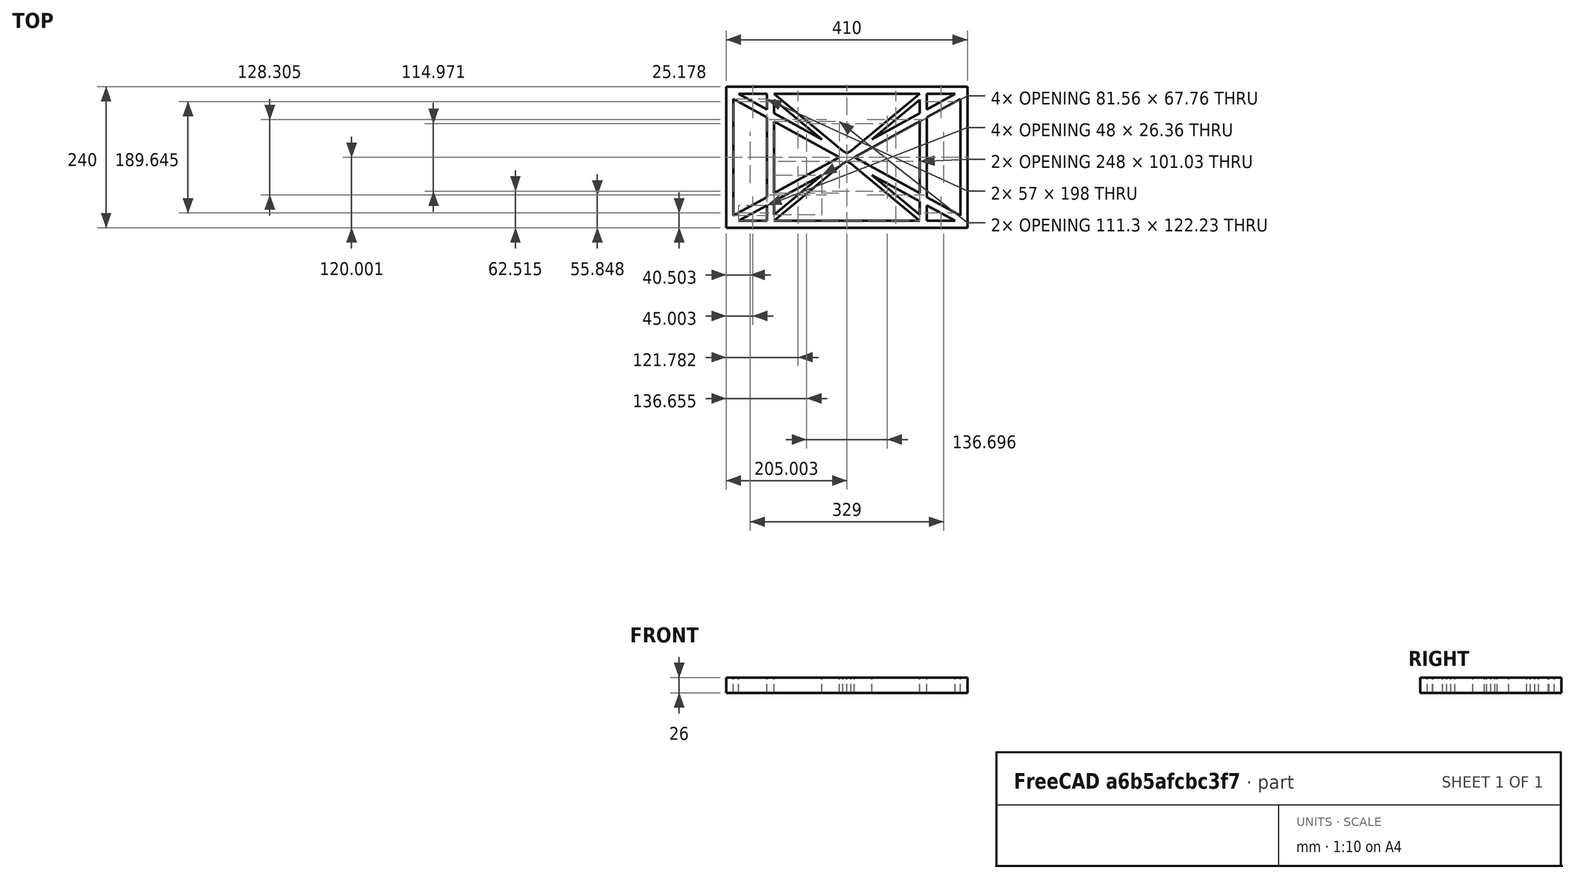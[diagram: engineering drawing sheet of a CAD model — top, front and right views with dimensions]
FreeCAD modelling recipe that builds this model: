
FCSTD DOCUMENT  (FreeCAD 0.19R0.19.2)
Label: laptopStand024
License: All rights reserved
LicenseURL: http://en.wikipedia.org/wiki/All_rights_reserved
objects: Sketcher::SketchObject×3, Part::Extrusion×1
note: 4 computed .brp shape members not serialized (recipe doc carries the construction recipe); baked Part::Feature solids carry a one-line shape summary decoded from their .brp

FEATURE [Sketcher::SketchObject] Sketch
  FullyConstrained = true
  sketch-geometry (52):
    g0: LineSegment StartX=-22.9272 StartY=136.221 StartZ=0 EndX=-22.9272 EndY=-103.779 EndZ=0
    g1: LineSegment StartX=-22.9272 StartY=136.221 StartZ=0 EndX=387.073 EndY=136.221 EndZ=0
    g2: LineSegment StartX=-22.9272 StartY=-103.779 StartZ=0 EndX=387.073 EndY=-103.779 EndZ=0
    g3: LineSegment StartX=387.073 StartY=136.221 StartZ=0 EndX=387.073 EndY=-103.779 EndZ=0
    g4: LineSegment StartX=375.073 StartY=115.221 StartZ=0 EndX=318.073 EndY=83.9235 EndZ=0
    g5: LineSegment StartX=-10.9272 StartY=-82.7794 StartZ=0 EndX=46.0728 EndY=-51.4823 EndZ=0
    g6: LineSegment StartX=-1.92719 StartY=124.221 StartZ=0 EndX=46.0728 EndY=97.8651 EndZ=0
    g7: LineSegment StartX=366.073 StartY=-91.7794 StartZ=0 EndX=318.073 EndY=-65.424 EndZ=0
    g8: LineSegment StartX=-10.9272 StartY=115.221 StartZ=0 EndX=-10.9272 EndY=-82.7794 EndZ=0
    g9: LineSegment StartX=375.073 StartY=-82.7794 StartZ=0 EndX=375.073 EndY=115.221 EndZ=0
    g10: LineSegment StartX=-1.92719 StartY=-91.7794 StartZ=0 EndX=46.0728 EndY=-91.7794 EndZ=0
    g11: LineSegment StartX=318.073 StartY=124.221 StartZ=0 EndX=366.073 EndY=124.221 EndZ=0
    g12: LineSegment StartX=306.073 StartY=-81.8102 StartZ=0 EndX=224.513 EndY=-14.0532 EndZ=0
    g13: LineSegment StartX=58.0728 StartY=114.251 StartZ=0 EndX=139.632 EndY=46.4944 EndZ=0
    g14: LineSegment StartX=306.073 StartY=124.221 StartZ=0 EndX=189.124 EndY=27.0628 EndZ=0
    g15: LineSegment StartX=58.0728 StartY=-91.7794 StartZ=0 EndX=175.022 EndY=5.37834 EndZ=0
    g16: LineSegment StartX=46.0728 StartY=124.221 StartZ=0 EndX=46.0728 EndY=97.8651 EndZ=0
    g17: LineSegment StartX=58.0728 StartY=-81.8102 StartZ=0 EndX=58.0728 EndY=-58.8351 EndZ=0
    g18: LineSegment StartX=318.073 StartY=124.221 StartZ=0 EndX=318.073 EndY=97.8651 EndZ=0
    g19: LineSegment StartX=306.073 StartY=114.251 StartZ=0 EndX=306.073 EndY=91.2763 EndZ=0
    g20: LineSegment StartX=182.073 StartY=23.1914 StartZ=0 EndX=189.124 EndY=27.0628 EndZ=0
    g21: LineSegment StartX=182.073 StartY=9.24976 StartZ=0 EndX=175.022 EndY=5.37834 EndZ=0
    g22: LineSegment StartX=224.513 StartY=46.4944 StartZ=0 EndX=306.073 EndY=114.251 EndZ=0
    g23: LineSegment StartX=175.022 StartY=27.0628 StartZ=0 EndX=58.0728 EndY=124.221 EndZ=0
    g24: LineSegment StartX=169.377 StartY=16.2206 StartZ=0 EndX=58.0728 EndY=77.3346 EndZ=0
    g25: LineSegment StartX=139.632 StartY=-14.0532 StartZ=0 EndX=58.0728 EndY=-81.8102 EndZ=0
    g26: LineSegment StartX=194.768 StartY=16.2206 StartZ=0 EndX=306.073 EndY=-44.8935 EndZ=0
    g27: LineSegment StartX=224.513 StartY=46.4944 StartZ=0 EndX=306.073 EndY=91.2763 EndZ=0
    g28: LineSegment StartX=175.022 StartY=27.0628 StartZ=0 EndX=182.073 EndY=23.1914 EndZ=0
    g29: LineSegment StartX=139.632 StartY=-14.0532 StartZ=0 EndX=58.0728 EndY=-58.8351 EndZ=0
    g30: LineSegment StartX=189.124 StartY=5.37834 StartZ=0 EndX=182.073 EndY=9.24976 EndZ=0
    g31: LineSegment StartX=189.124 StartY=5.37834 StartZ=0 EndX=306.073 EndY=-91.7794 EndZ=0
    g32: LineSegment StartX=306.073 StartY=77.3346 StartZ=0 EndX=306.073 EndY=-44.8935 EndZ=0
    g33: LineSegment StartX=318.073 StartY=83.9235 StartZ=0 EndX=318.073 EndY=-51.4823 EndZ=0
    g34: LineSegment StartX=318.073 StartY=97.8651 StartZ=0 EndX=366.073 EndY=124.221 EndZ=0
    g35: LineSegment StartX=306.073 StartY=77.3346 StartZ=0 EndX=194.768 EndY=16.2206 EndZ=0
    g36: LineSegment StartX=306.073 StartY=-58.8351 StartZ=0 EndX=224.513 EndY=-14.0532 EndZ=0
    g37: LineSegment StartX=306.073 StartY=-58.8351 StartZ=0 EndX=306.073 EndY=-81.8102 EndZ=0
    g38: LineSegment StartX=318.073 StartY=-51.4823 StartZ=0 EndX=375.073 EndY=-82.7794 EndZ=0
    g39: LineSegment StartX=318.073 StartY=-65.424 StartZ=0 EndX=318.073 EndY=-91.7794 EndZ=0
    g40: LineSegment StartX=306.073 StartY=124.221 StartZ=0 EndX=58.0728 EndY=124.221 EndZ=0
    g41: LineSegment StartX=318.073 StartY=-91.7794 StartZ=0 EndX=366.073 EndY=-91.7794 EndZ=0
    g42: LineSegment StartX=58.0728 StartY=-91.7794 StartZ=0 EndX=306.073 EndY=-91.7794 EndZ=0
    g43: LineSegment StartX=58.0728 StartY=-44.8935 StartZ=0 EndX=58.0728 EndY=77.3346 EndZ=0
    g44: LineSegment StartX=46.0728 StartY=-65.424 StartZ=0 EndX=-1.92719 EndY=-91.7794 EndZ=0
    g45: LineSegment StartX=46.0728 StartY=-65.424 StartZ=0 EndX=46.0728 EndY=-91.7794 EndZ=0
    g46: LineSegment StartX=58.0728 StartY=-44.8935 StartZ=0 EndX=169.377 EndY=16.2206 EndZ=0
    g47: LineSegment StartX=58.0728 StartY=91.2763 StartZ=0 EndX=58.0728 EndY=114.251 EndZ=0
    g48: LineSegment StartX=46.0728 StartY=83.9235 StartZ=0 EndX=46.0728 EndY=-51.4823 EndZ=0
    g49: LineSegment StartX=46.0728 StartY=124.221 StartZ=0 EndX=-1.92719 EndY=124.221 EndZ=0
    g50: LineSegment StartX=58.0728 StartY=91.2763 StartZ=0 EndX=139.632 EndY=46.4944 EndZ=0
    g51: LineSegment StartX=46.0728 StartY=83.9235 StartZ=0 EndX=-10.9272 EndY=115.221 EndZ=0
  constraints (102):
    c: Vertical(g0)
    c: Distance(g0) = 240
    c: Horizontal(g1)
    c: Distance(g1) = 410
    c: Coincident(g1,g0)
    c: Coincident(g2,g0)
    c: Horizontal(g2)
    c: Coincident(g3,g1)
    c: Vertical(g3)
    c: Coincident(g2,g3)
    c: Block(g1)
    c: Horizontal(g10)
    c: Horizontal(g11)
    c: PointOnObject(g35,g6)
    c: Coincident(g28,g20)
    c: Coincident(g30,g21)
    c: Tangent(g7,g24)
    c: PointOnObject(g24,g5)
    c: PointOnObject(g26,g4)
    c: Coincident(g20,g14)
    c: Tangent(g20,g27)
    c: Coincident(g50,g13)
    c: Coincident(g28,g23)
    c: Coincident(g22,g27)
    c: Coincident(g21,g15)
    c: Coincident(g29,g25)
    c: Tangent(g21,g29)
    c: Coincident(g36,g12)
    c: Coincident(g31,g30)
    c: Coincident(g22,g19)
    c: Tangent(g19,g32)
    c: Tangent(g18,g33)
    c: Coincident(g27,g19)
    c: Tangent(g27,g34)
    c: Coincident(g4,g33)
    c: Coincident(g35,g32)
    c: Tangent(g4,g35)
    c: Coincident(g37,g12)
    c: Tangent(g7,g36)
    c: Tangent(g32,g37)
    c: Coincident(g26,g32)
    c: Tangent(g26,g38)
    c: Coincident(g33,g38)
    c: Coincident(g39,g7)
    c: Tangent(g33,g39)
    c: Coincident(g25,g17)
    c: Tangent(g17,g43)
    c: Coincident(g29,g17)
    c: Tangent(g29,g44)
    c: Coincident(g45,g44)
    c: Tangent(g16,g45)
    c: Coincident(g5,g48)
    c: Coincident(g46,g43)
    c: Tangent(g5,g46)
    c: Tangent(g43,g47)
    c: Tangent(g16,g48)
    c: Coincident(g13,g47)
    c: PointOnObject(g40,g23)
    c: Tangent(g40,g49)
    c: Coincident(g6,g16)
    c: Coincident(g50,g47)
    c: Tangent(g6,g50)
    c: Coincident(g24,g43)
    c: Coincident(g51,g48)
    c: Tangent(g24,g51)
    c: Block(g23)
    c: Block(g14)
    c: Block(g20)
    c: Block(g40)
    c: Block(g18)
    c: Block(g34)
    c: Block(g4)
    c: Block(g38)
    c: Block(g9)
    c: Block(g36)
    c: Block(g37)
    c: Block(g7)
    c: Block(g39)
    c: Block(g22)
    c: Block(g31)
    c: Block(g42)
    c: Block(g21)
    c: Block(g15)
    c: Block(g29)
    c: Block(g25)
    c: Block(g45)
    c: Block(g44)
    c: Block(g5)
    c: Block(g8)
    c: Block(g51)
    c: Block(g6)
    c: Block(g16)
    c: Block(g13)
    c: Block(g47)
    c: Block(g35)
    c: Block(g32)
    c: Block(g24)
    c: Block(g46)
    c: Block(g49)
    c: Block(g11)
    c: Block(g41)
    c: Block(g10)
FEATURE [Part::Extrusion] Extrude
  Base = -> Sketch
  Dir = (0,0,1)
  DirMode = 2
  FaceMakerClass = Part::FaceMakerBullseye
  LengthFwd = 26
  LengthRev = 0
  Solid = true
  Symmetric = false
FEATURE [Sketcher::SketchObject] Sketch001
  FullyConstrained = false
  MapMode = 4
  Placement = pos=(0,0,0) rot=(0.57735,0.57735,0.57735;2.0944rad)
  Support = -> [Sketch]
  sketch-geometry (22):
    g0: LineSegment StartX=17.2228 StartY=-16.0875 StartZ=0 EndX=117.223 EndY=-16.0875 EndZ=0
    g1: LineSegment StartX=17.2228 StartY=-16.0875 StartZ=0 EndX=17.2228 EndY=-19.0875 EndZ=0
    g2: LineSegment StartX=117.223 StartY=-16.0875 StartZ=0 EndX=117.223 EndY=-19.0875 EndZ=0
    g3: BSplineCurve PolesCount=3 KnotsCount=2 Degree=2 IsPeriodic=0
    g4: LineSegment StartX=94.6577 StartY=-26.1351 StartZ=0 EndX=24.2583 EndY=-213.335 EndZ=0
    g5: LineSegment StartX=-9.4377 StartY=-200.664 StartZ=0 EndX=24.2583 EndY=-213.335 EndZ=0
    g6: LineSegment StartX=-9.4377 StartY=-200.664 StartZ=0 EndX=56.1962 EndY=-26.1351 EndZ=0
    g7: LineSegment StartX=17.2228 StartY=-19.0875 StartZ=0 EndX=38.8094 EndY=-19.0875 EndZ=0
    g8: BSplineCurve PolesCount=4 KnotsCount=2 Degree=3 IsPeriodic=0
    g9: LineSegment StartX=78.0148 StartY=-19.2805 StartZ=0 EndX=73.122 EndY=-32.2909 EndZ=0
    g10: ArcOfCircle CenterX=73.122 CenterY=-32.2909 CenterZ=0 NormalX=0 NormalY=0 NormalZ=1 AngleXU=0 Radius=13 StartAngle=5.92268 EndAngle=9.06428
    g11: LineSegment StartX=73.122 StartY=-32.2909 StartZ=0 EndX=77.698 EndY=-20.1229 EndZ=0
    g12: LineSegment StartX=73.122 StartY=-32.2909 StartZ=0 EndX=65.0089 EndY=-53.8124 EndZ=0
    g13: LineSegment StartX=65.0089 StartY=-53.8124 StartZ=0 EndX=58.4618 EndY=-71.2221 EndZ=0
    g14: LineSegment StartX=85.2864 StartY=-36.8765 StartZ=0 EndX=78.9505 EndY=-53.7246 EndZ=0
    g15: LineSegment StartX=60.9577 StartY=-27.7052 StartZ=0 EndX=54.6217 EndY=-44.5532 EndZ=0
    g16: ArcOfCircle CenterX=66.7842 CenterY=-49.1439 CenterZ=0 NormalX=0 NormalY=0 NormalZ=1 AngleXU=0 Radius=13 StartAngle=2.78068 EndAngle=5.92131
    g17: ArcOfCircle CenterX=97.2888 CenterY=-81.8271 CenterZ=0 NormalX=0 NormalY=0 NormalZ=1 AngleXU=0 Radius=13 StartAngle=5.92268 EndAngle=9.06428
    g18: LineSegment StartX=102.182 StartY=-68.8167 StartZ=0 EndX=97.2888 EndY=-81.8271 EndZ=0
    g19: LineSegment StartX=85.1244 StartY=-77.2415 StartZ=0 EndX=78.7885 EndY=-94.0895 EndZ=0
    g20: ArcOfCircle CenterX=90.9509 CenterY=-98.6802 CenterZ=0 NormalX=0 NormalY=0 NormalZ=1 AngleXU=0 Radius=13 StartAngle=2.78068 EndAngle=5.92131
    g21: LineSegment StartX=109.453 StartY=-86.4128 StartZ=0 EndX=103.117 EndY=-103.261 EndZ=0
  constraints (45):
    c: Horizontal(g0)
    c: Distance(g0) = 100
    c: Block(g0)
    c: Coincident(g1,g0)
    c: Vertical(g1)
    c: Distance(g1) = 3
    c: Coincident(g2,g0)
    c: Vertical(g2)
    c: Distance(g2) = 3
    c: Block(g3)
    c: Coincident(g3,g2)
    c: Coincident(g4,g3)
    c: Block(g4)
    c: Coincident(g5,g4)
    c: Coincident(g6,g5)
    c: Coincident(g7,g1)
    c: Horizontal(g7)
    c: Block(g8)
    c: Coincident(g8,g7)
    c: Coincident(g8,g6)
    c: Block(g6)
    c: Block(g10)
    c: Coincident(g11,g10)
    c: PointOnObject(g11,g10)
    c: Coincident(g11,g9)
    c: Block(g9)
    c: Coincident(g12,g9)
    c: Coincident(g13,g12)
    c: Distance(g13) = 18.6
    c: Parallel(g4,g13)
    c: Distance(g14) = 18
    c: Coincident(g14,g10)
    c: Parallel(g4,g14)
    c: Coincident(g15,g10)
    c: Block(g16)
    c: Coincident(g16,g15)
    c: Block(g15)
    c: Block(g17)
    c: Block(g18)
    c: Equal(g14,g21) = 18
    c: Coincident(g21,g17)
    c: Coincident(g19,g17)
    c: Block(g20)
    c: Coincident(g20,g19)
    c: Block(g19)
FEATURE [Sketcher::SketchObject] Sketch002
  FullyConstrained = true
  Placement = pos=(0,0,0) rot=(-1,0,0;4.71239rad)
